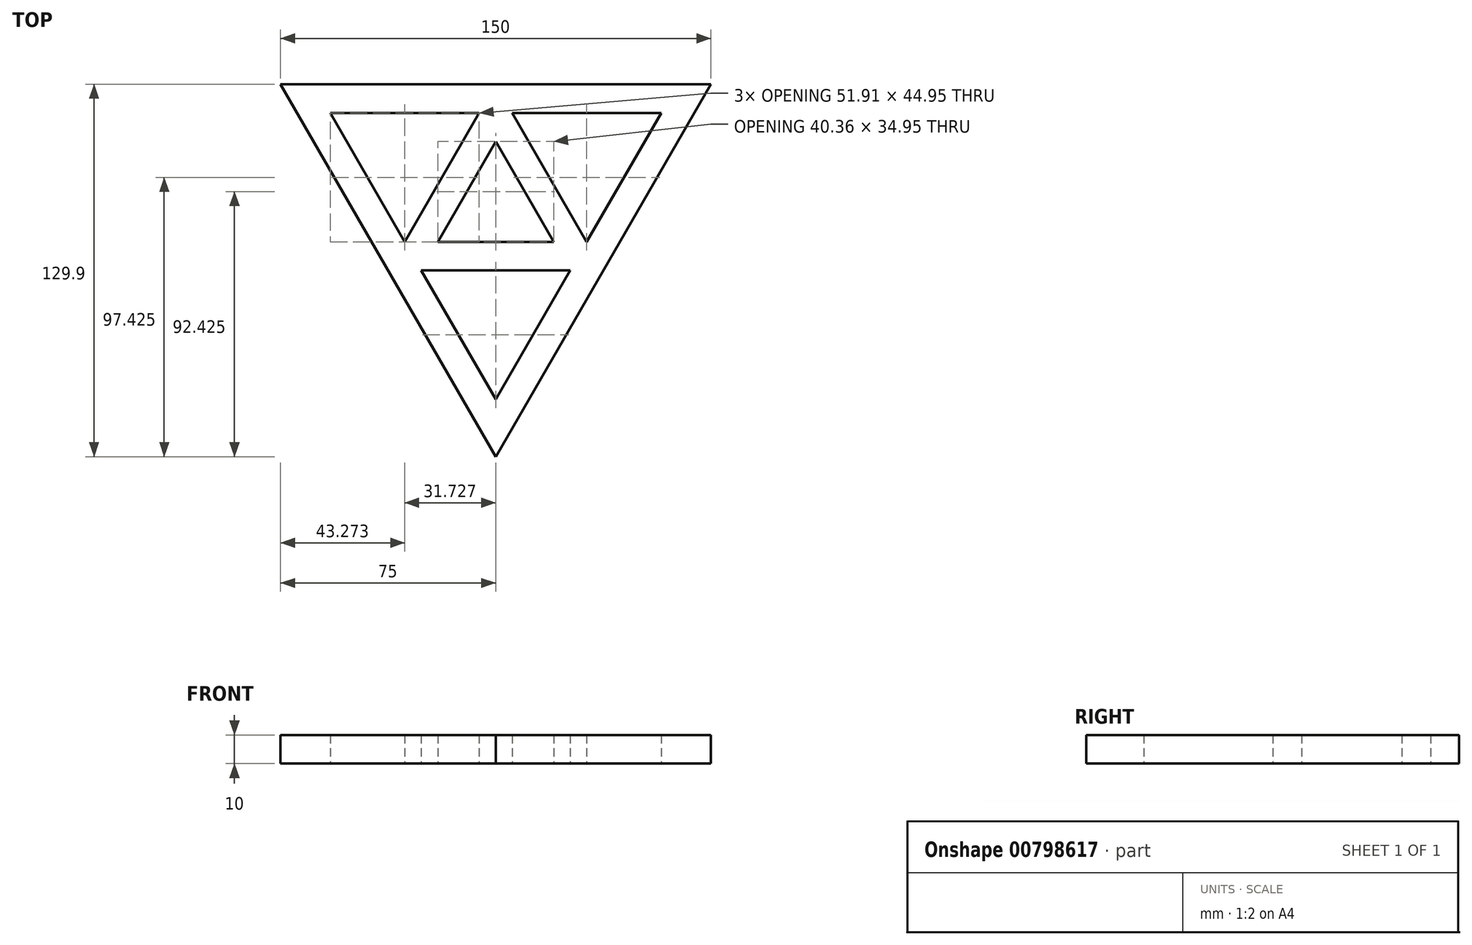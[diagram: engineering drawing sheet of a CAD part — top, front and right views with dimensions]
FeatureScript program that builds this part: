
annotation { "Feature Type Name" : "Feature", "Feature Type Description" : "" }
export const myFeature = defineFeature(function(context is Context, id is Id, definition is map)
    precondition{}
    {
        {
            var Q0;
            Q0=qCreatedBy(makeId("Top.planeOp"),FACE);
            var sketch = newSketch(context, id + "F0", { "sketchPlane" : qUnion([Q0])});
            skCircle(sketch, "E0.cCircle", {"center": v(0, 0) * mm, "radius": 43.3 * mm, "construction": true});
            skLineSegment(sketch, "E0.0", {"start": v(-75, 43.3) * mm, "end": v(75, 43.3) * mm});
            skLineSegment(sketch, "E0.1", {"start": v(75, 43.3) * mm, "end": v(0, -86.6) * mm});
            skLineSegment(sketch, "E0.2", {"start": v(0, -86.6) * mm, "end": v(-75, 43.3) * mm});
            skPoint(sketch, "E0.0.midPoint", {"position": v(0, 43.3) * mm});
            skLineSegment(sketch, "E1.0", {"start": v(-57.68, 33.3) * mm, "end": v(57.68, 33.3) * mm});
            skLineSegment(sketch, "E1.1", {"start": v(0, -66.6) * mm, "end": v(-57.68, 33.3) * mm});
            skLineSegment(sketch, "E1.2", {"start": v(57.68, 33.3) * mm, "end": v(0, -66.6) * mm});
            skLineSegment(sketch, "E2", {"start": v(75, 43.3) * mm, "end": v(-37.5, -21.65) * mm});
            skLineSegment(sketch, "E3", {"start": v(-37.5, -21.65) * mm, "end": v(37.5, -21.65) * mm});
            skLineSegment(sketch, "E4", {"start": v(-37.5, -21.65) * mm, "end": v(0, 43.3) * mm});
            skLineSegment(sketch, "E5", {"start": v(0, 43.3) * mm, "end": v(37.5, -21.65) * mm});
            skLineSegment(sketch, "E6.0", {"start": v(-20.18, -11.65) * mm, "end": v(0, 23.3) * mm});
            skLineSegment(sketch, "E6.1", {"start": v(-20.18, -11.65) * mm, "end": v(20.18, -11.65) * mm});
            skLineSegment(sketch, "E6.2", {"start": v(0, 23.3) * mm, "end": v(20.18, -11.65) * mm});
            skSolve(sketch);
        }
        {
            var Q0;
            {var subQ0=sQuery(id+"F0.wireOp",EDGE,"E1.1");var subQ1=sQuery(id+"F0.wireOp",EDGE,"E1.0");var subQ2=makeQuery(id+"F0.imprint","INTERSECT",VERTEX,{"derivedFrom":[subQ1,subQ0]});Q0=makeQuery(id+"F0.imprint","IMPRINT",FACE,{"disambiguationData":[TD([[makeQuery(id+"F0.imprint","IMPRINT",EDGE,{"disambiguationData":[TD([[subQ2,-1.0]])],"derivedFrom":subQ1}),1.0]])]});}
            var Q1;
            {var subQ0=sQuery(id+"F0.wireOp",EDGE,"E6.0");Q1=makeQuery(id+"F0.imprint","IMPRINT",FACE,{"disambiguationData":[TD([[makeQuery(id+"F0.imprint","IMPRINT",EDGE,{"derivedFrom":subQ0}),1.0]])]});}
            var Q2;
            {var subQ0=sQuery(id+"F0.wireOp",EDGE,"E4");var subQ1=sQuery(id+"F0.wireOp",EDGE,"E1.0");var subQ2=makeQuery(id+"F0.imprint","INTERSECT",VERTEX,{"derivedFrom":[subQ1,subQ0]});Q2=makeQuery(id+"F0.imprint","IMPRINT",FACE,{"disambiguationData":[TD([[makeQuery(id+"F0.imprint","IMPRINT",EDGE,{"disambiguationData":[TD([[subQ2,-1.0]])],"derivedFrom":subQ1}),1.0]])]});}
            var Q3;
            {var subQ3=sQuery(id+"F0.wireOp",EDGE,"E5");var subQ5=sQuery(id+"F0.wireOp",EDGE,"E1.0");var subQ7=makeQuery(id+"F0.imprint","INTERSECT",VERTEX,{"derivedFrom":[subQ5,subQ3]});Q3=makeQuery(id+"F0.imprint","IMPRINT",FACE,{"disambiguationData":[TD([[makeQuery(id+"F0.imprint","IMPRINT",EDGE,{"disambiguationData":[TD([[subQ7,-1.0]])],"derivedFrom":subQ5}),1.0]])]});}
            var Q4;
            {var subQ9=sQuery(id+"F0.wireOp",EDGE,"E6.1");Q4=makeQuery(id+"F0.imprint","IMPRINT",FACE,{"disambiguationData":[TD([[makeQuery(id+"F0.imprint","IMPRINT",EDGE,{"derivedFrom":subQ9}),-1.0]])]});}
            var Q5;
            {var subQ3=sQuery(id+"F0.wireOp",EDGE,"E5");var subQ5=sQuery(id+"F0.wireOp",EDGE,"E1.2");var subQ7=makeQuery(id+"F0.imprint","INTERSECT",VERTEX,{"derivedFrom":[subQ5,subQ3]});Q5=makeQuery(id+"F0.imprint","IMPRINT",FACE,{"disambiguationData":[TD([[makeQuery(id+"F0.imprint","IMPRINT",EDGE,{"disambiguationData":[TD([[subQ7,1.0]])],"derivedFrom":subQ5}),1.0]])]});}
            var Q6;
            {var subQ0=sQuery(id+"F0.wireOp",EDGE,"E5");var subQ1=sQuery(id+"F0.wireOp",EDGE,"E1.2");var subQ2=makeQuery(id+"F0.imprint","INTERSECT",VERTEX,{"derivedFrom":[subQ1,subQ0]});Q6=makeQuery(id+"F0.imprint","IMPRINT",FACE,{"disambiguationData":[TD([[makeQuery(id+"F0.imprint","IMPRINT",EDGE,{"disambiguationData":[TD([[subQ2,-1.0]])],"derivedFrom":subQ1}),1.0]])]});}
            var Q7;
            {var subQ0=sQuery(id+"F0.wireOp",EDGE,"E1.2");var subQ1=sQuery(id+"F0.wireOp",EDGE,"E1.1");var subQ2=makeQuery(id+"F0.imprint","INTERSECT",VERTEX,{"derivedFrom":[subQ1,subQ0]});Q7=makeQuery(id+"F0.imprint","IMPRINT",FACE,{"disambiguationData":[TD([[makeQuery(id+"F0.imprint","IMPRINT",EDGE,{"disambiguationData":[TD([[subQ2,-1.0]])],"derivedFrom":subQ1}),1.0]])]});}
            var Q8;
            {var subQ0=sQuery(id+"F0.wireOp",EDGE,"E2");var subQ1=sQuery(id+"F0.wireOp",EDGE,"E1.1");var subQ2=makeQuery(id+"F0.imprint","INTERSECT",VERTEX,{"derivedFrom":[subQ1,subQ0]});Q8=makeQuery(id+"F0.imprint","IMPRINT",FACE,{"disambiguationData":[TD([[makeQuery(id+"F0.imprint","IMPRINT",EDGE,{"disambiguationData":[TD([[subQ2,-1.0]])],"derivedFrom":subQ1}),1.0]])]});}
            var Q9;
            {var subQ0=sQuery(id+"F0.wireOp",EDGE,"E3");var subQ1=sQuery(id+"F0.wireOp",EDGE,"E1.1");var subQ2=makeQuery(id+"F0.imprint","INTERSECT",VERTEX,{"derivedFrom":[subQ1,subQ0]});Q9=makeQuery(id+"F0.imprint","IMPRINT",FACE,{"disambiguationData":[TD([[makeQuery(id+"F0.imprint","IMPRINT",EDGE,{"disambiguationData":[TD([[subQ2,-1.0]])],"derivedFrom":subQ1}),1.0]])]});}
            extrude(context, id + "F1", {"entities" : qUnion([Q0, Q1, Q2, Q3, Q4, Q5, Q6, Q7, Q8, Q9]), "depth" : 10 * mm, "offsetDistance" : 25 * mm});
        }
    });
